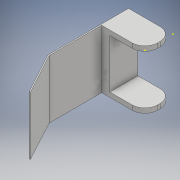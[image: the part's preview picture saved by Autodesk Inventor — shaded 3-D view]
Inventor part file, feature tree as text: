
AUTODESK INVENTOR PART (.ipt)
format: ipt  version: 2017 (Build 210142000, 142)  size: 149,504 bytes
history: native  units: mm
features: sketch x10, extrude x4, chamfer x2, other x1, fillet x1
ambient origin geometry x8: Origin, YZ Plane, XZ Plane, XY Plane, X Axis, Y Axis, Z Axis, Center Point
bodies: Body1 (feature_tree)
feature tree (18):
  other  "ソリッド1"
  extrude  "押し出し1"  Depth=0.37mm
  sketch  "スケッチ2"
  sketch  "スケッチ3"
  sketch  "スケッチ4"
  fillet  "フィレット1"  Radius=0.04mm
  extrude  "押し出し2"  Depth=0.07mm
  extrude  "押し出し3"  Depth=0.42mm
  extrude  "押し出し4"  Depth=0.04mm
  sketch  "スケッチ8"
  sketch  "スケッチ9"
  sketch  "スケッチ10"
  chamfer  "面取り1"  Distance=0.24mm
  chamfer  "面取り2"  Distance=0.11mm
  sketch  "スケッチ1"
  sketch  "スケッチ5"
  sketch  "スケッチ6"
  sketch  "スケッチ7"
